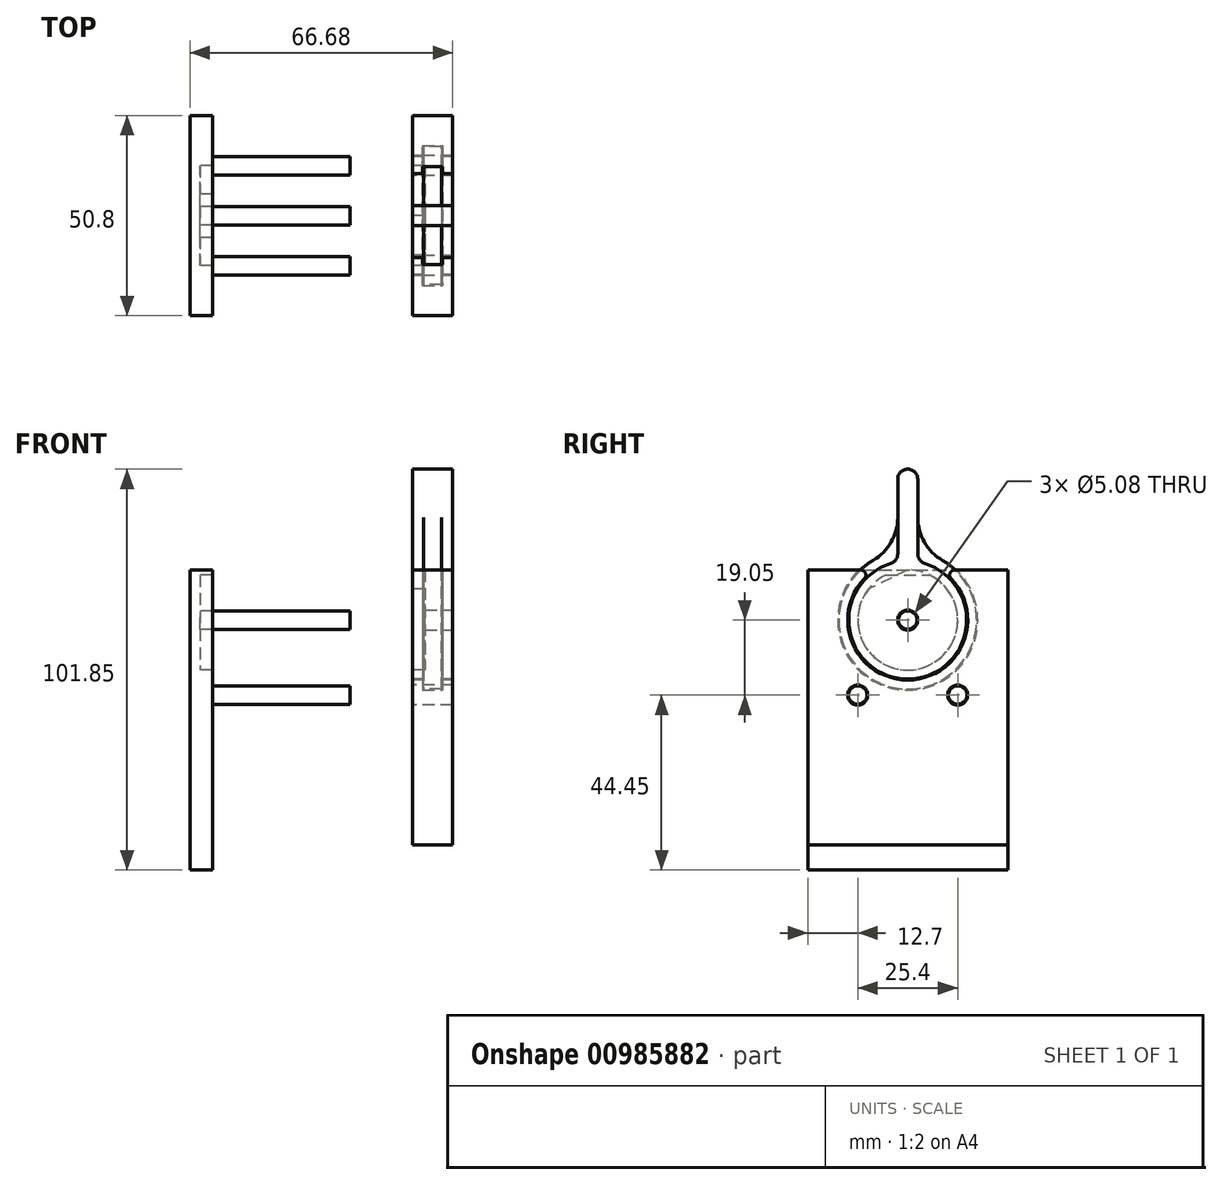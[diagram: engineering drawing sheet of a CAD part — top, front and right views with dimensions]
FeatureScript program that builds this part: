
annotation { "Feature Type Name" : "Feature", "Feature Type Description" : "" }
export const myFeature = defineFeature(function(context is Context, id is Id, definition is map)
    precondition{}
    {
        {
            var Q0;
            Q0=qCreatedBy(makeId("Right.planeOp"),FACE);
            var sketch = newSketch(context, id + "F0", { "sketchPlane" : qUnion([Q0])});
            skCircle(sketch, "E0", {"center": v(0, 0) * mm, "radius": 2.35 * mm});
            skSolve(sketch);
        }
        {
            var Q0;
            Q0=makeQuery(id+"F0.imprint","IMPRINT",FACE,{"disambiguationData":[TD([[makeQuery(id+"F0.imprint","IMPRINT",EDGE,{"derivedFrom":sQuery(id+"F0.wireOp",EDGE,"E0")}),1.0]])]});
            extrude(context, id + "F1", {"entities" : qUnion([Q0]), "depth" : 38.1 * mm, "offsetDistance" : 25.4 * mm});
        }
        {
            var Q0;
            Q0=qCreatedBy(makeId("Right.planeOp"),FACE);
            var sketch = newSketch(context, id + "F2", { "sketchPlane" : qUnion([Q0])});
            skLineSegment(sketch, "E1.bottom", {"start": v(-25.4, -63.5) * mm, "end": v(25.4, -63.5) * mm});
            skLineSegment(sketch, "E1.top", {"start": v(-25.4, 12.7) * mm, "end": v(25.4, 12.7) * mm});
            skLineSegment(sketch, "E1.left", {"start": v(-25.4, -63.5) * mm, "end": v(-25.4, 12.7) * mm});
            skLineSegment(sketch, "E1.right", {"start": v(25.4, -63.5) * mm, "end": v(25.4, 12.7) * mm});
            skSolve(sketch);
        }
        {
            var Q0;
            Q0=makeQuery(id+"F2.imprint","IMPRINT",FACE,{"disambiguationData":[TD([[makeQuery(id+"F2.imprint","IMPRINT",EDGE,{"derivedFrom":sQuery(id+"F2.wireOp",EDGE,"E1.bottom")}),1.0]])]});
            extrude(context, id + "F3", {"entities" : qUnion([Q0]), "operationType" : NewBodyOperationType.ADD, "oppositeDirection" : true, "depth" : 2.54 * mm, "offsetDistance" : 25.4 * mm});
        }
        {
            var Q0;
            Q0=makeQuery(id+"F3.opExtrude","CAP_FACE",FACE,{"disambiguationData":[OSD([sQuery(id+"F2.wireOp",EDGE,"E1.bottom"),sQuery(id+"F2.wireOp",EDGE,"E1.top"),sQuery(id+"F2.wireOp",EDGE,"E1.left"),sQuery(id+"F2.wireOp",EDGE,"E1.right")])],"isStart":true});
            var sketch = newSketch(context, id + "F4", { "sketchPlane" : qUnion([Q0])});
            skCircle(sketch, "E2", {"center": v(0, 0) * mm, "radius": 12.7 * mm});
            skLineSegment(sketch, "E3", {"start": v(-5.54, 11.43) * mm, "end": v(5.54, 11.43) * mm});
            skSolve(sketch);
        }
        {
            var Q0;
            Q0=makeQuery(id+"F4.imprint","IMPRINT",FACE,{"disambiguationData":[TD([[makeQuery(id+"F4.imprint","IMPRINT",EDGE,{"derivedFrom":makeQuery(id+"F3.opExtrude","CAP_EDGE",EDGE,{"disambiguationData":[OSD([sQuery(id+"F2.wireOp",EDGE,"E1.bottom")])],"isStart":true})}),1.0]])]});
            var Q1;
            {var subQ0=sQuery(id+"F4.wireOp",EDGE,"E3");Q1=makeQuery(id+"F4.imprint","IMPRINT",FACE,{"disambiguationData":[TD([[makeQuery(id+"F4.imprint","IMPRINT",EDGE,{"derivedFrom":subQ0}),1.0]])]});}
            extrude(context, id + "F5", {"entities" : qUnion([Q0, Q1]), "operationType" : NewBodyOperationType.ADD, "depth" : 3.17 * mm, "offsetDistance" : 25.4 * mm});
        }
        {
            var Q0;
            Q0=makeQuery(id+"F5.opExtrude","CAP_FACE",FACE,{"disambiguationData":[OSD([sQuery(id+"F2.wireOp",EDGE,"E1.bottom"),sQuery(id+"F2.wireOp",EDGE,"E1.top"),sQuery(id+"F2.wireOp",EDGE,"E1.left"),sQuery(id+"F2.wireOp",EDGE,"E1.right"),sQuery(id+"F4.wireOp",EDGE,"E2"),sQuery(id+"F4.wireOp",EDGE,"E3")])],"isStart":false});
            var sketch = newSketch(context, id + "F6", { "sketchPlane" : qUnion([Q0])});
            skCircle(sketch, "E4", {"center": v(-12.7, -19.05) * mm, "radius": 2.35 * mm});
            skCircle(sketch, "E5", {"center": v(12.7, -19.05) * mm, "radius": 2.35 * mm});
            skSolve(sketch);
        }
        {
            var Q0;
            Q0=makeQuery(id+"F6.imprint","IMPRINT",FACE,{"disambiguationData":[TD([[makeQuery(id+"F6.imprint","IMPRINT",EDGE,{"derivedFrom":sQuery(id+"F6.wireOp",EDGE,"E4")}),1.0]])]});
            var Q1;
            Q1=makeQuery(id+"F6.imprint","IMPRINT",FACE,{"disambiguationData":[TD([[makeQuery(id+"F6.imprint","IMPRINT",EDGE,{"derivedFrom":sQuery(id+"F6.wireOp",EDGE,"E5")}),1.0]])]});
            var Q2;
            Q2=makeQuery(id+"F1.opExtrude","CAP_FACE",FACE,{"disambiguationData":[OSD([sQuery(id+"F0.wireOp",EDGE,"E0")])],"isStart":false});
            extrude(context, id + "F7", {"entities" : qUnion([Q0, Q1]), "operationType" : NewBodyOperationType.ADD, "endBound" : BoundingType.UP_TO_SURFACE, "depth" : 25.4 * mm, "endBoundEntityFace" : qUnion([Q2]), "offsetDistance" : 25.4 * mm});
        }
        {
            var Q0;
            Q0=makeQuery(id+"F5.opExtrude","CAP_FACE",FACE,{"disambiguationData":[OSD([sQuery(id+"F2.wireOp",EDGE,"E1.bottom"),sQuery(id+"F2.wireOp",EDGE,"E1.top"),sQuery(id+"F2.wireOp",EDGE,"E1.left"),sQuery(id+"F2.wireOp",EDGE,"E1.right"),sQuery(id+"F4.wireOp",EDGE,"E2"),sQuery(id+"F4.wireOp",EDGE,"E3")])],"isStart":false});
            cPlane(context, id + "F8", {"entities" : qUnion([Q0]), "cplaneType" : CPlaneType.OFFSET, "offset" : 50.8 * mm, "width" : 152.4 * mm, "height" : 152.4 * mm});
        }
        {
            var Q0;
            Q0=qCreatedBy(id+"F8.planeOp",FACE);
            var sketch = newSketch(context, id + "F9", { "sketchPlane" : qUnion([Q0])});
            skLineSegment(sketch, "E6.bottom", {"start": v(-25.4, -57.15) * mm, "end": v(25.4, -57.15) * mm});
            skLineSegment(sketch, "E6.top", {"start": v(-25.4, 12.7) * mm, "end": v(25.4, 12.7) * mm});
            skLineSegment(sketch, "E6.left", {"start": v(-25.4, -57.15) * mm, "end": v(-25.4, 12.7) * mm});
            skLineSegment(sketch, "E6.right", {"start": v(25.4, -57.15) * mm, "end": v(25.4, 12.7) * mm});
            skCircle(sketch, "E7.0", {"center": v(0, 0) * mm, "radius": 2.35 * mm});
            skCircle(sketch, "E8.0.0", {"center": v(12.7, -19.05) * mm, "radius": 2.35 * mm});
            skCircle(sketch, "E9.0.0", {"center": v(-12.7, -19.05) * mm, "radius": 2.35 * mm});
            skCircle(sketch, "E10", {"center": v(12.7, -19.05) * mm, "radius": 2.54 * mm});
            skCircle(sketch, "E11", {"center": v(-12.7, -19.05) * mm, "radius": 2.54 * mm});
            skCircle(sketch, "E12", {"center": v(0, 0) * mm, "radius": 15.24 * mm});
            skSolve(sketch);
        }
        {
            var Q0;
            Q0=makeQuery(id+"F9.imprint","IMPRINT",FACE,{"disambiguationData":[TD([[makeQuery(id+"F9.imprint","IMPRINT",EDGE,{"derivedFrom":sQuery(id+"F9.wireOp",EDGE,"E6.bottom")}),1.0]])]});
            extrude(context, id + "F10", {"entities" : qUnion([Q0]), "depth" : 10.16 * mm, "offsetDistance" : 25.4 * mm});
        }
        {
            var Q0;
            {var subQ0=sQuery(id+"F9.wireOp",EDGE,"E12");var subQ1=sQuery(id+"F9.wireOp",EDGE,"E6.top");Q0=makeQuery(id+"F10.opExtrude","SWEPT_EDGE",EDGE,{"disambiguationData":[OSD([subQ1,subQ0]),TDD([makeQuery(id+"F9.imprint","INTERSECT",VERTEX,{"disambiguationData":[OD(1.0)],"derivedFrom":[subQ1,subQ0]})])]});}
            var Q1;
            {var subQ0=sQuery(id+"F9.wireOp",EDGE,"E12");var subQ1=sQuery(id+"F9.wireOp",EDGE,"E6.top");Q1=makeQuery(id+"F10.opExtrude","SWEPT_EDGE",EDGE,{"disambiguationData":[OSD([subQ1,subQ0]),TDD([makeQuery(id+"F9.imprint","INTERSECT",VERTEX,{"disambiguationData":[OD(0.0)],"derivedFrom":[subQ1,subQ0]})])]});}
            fillet(context, id + "F11", {"entities" : qUnion([Q0, Q1]), "radius" : 1.27 * mm, "tangentPropagation" : true, "allowEdgeOverflow" : false});
        }
        {
            var Q0;
            Q0=qCreatedBy(makeId("Top.planeOp"),FACE);
            var sketch = newSketch(context, id + "F12", { "sketchPlane" : qUnion([Q0])});
            skLineSegment(sketch, "E13.bottom", {"start": v(56.52, 17.78) * mm, "end": v(61.6, 17.78) * mm});
            skLineSegment(sketch, "E13.top", {"start": v(56.52, 8.52) * mm, "end": v(61.6, 8.52) * mm});
            skLineSegment(sketch, "E13.left", {"start": v(56.52, 17.78) * mm, "end": v(56.52, 8.52) * mm});
            skLineSegment(sketch, "E13.right", {"start": v(61.6, 17.78) * mm, "end": v(61.6, 8.52) * mm});
            skLineSegment(sketch, "E14", {"start": v(30.1, 15.24) * mm, "end": v(40.26, 15.24) * mm});
            skLineSegment(sketch, "E15", {"start": v(0, 2.35) * mm, "end": v(38.1, 2.35) * mm});
            skLineSegment(sketch, "E16", {"start": v(38.1, -2.35) * mm, "end": v(0, -2.35) * mm});
            skPoint(sketch, "E17.0", {"position": v(0, 0) * mm});
            skLineSegment(sketch, "E18", {"start": v(0, 0) * mm, "end": v(56.77, 0) * mm, "construction": true});
            skSolve(sketch);
        }
        {
            var Q0;
            {var subQ0=sQuery(id+"F12.wireOp",EDGE,"E13.bottom");Q0=makeQuery(id+"F12.imprint","IMPRINT",FACE,{"disambiguationData":[TD([[makeQuery(id+"F12.imprint","IMPRINT",EDGE,{"derivedFrom":subQ0}),-1.0]])]});}
            var Q1;
            Q1=sQuery(id+"F12.wireOp",EDGE,"E18");
            revolve(context, id + "F13", {"operationType" : NewBodyOperationType.REMOVE, "surfaceOperationType" : NewSurfaceOperationType.NEW, "entities" : qUnion([Q0]), "axis" : qUnion([Q1]), "revolveType" : RevolveType.FULL, "oppositeDirection" : true});
        }
        {
            var Q0;
            Q0=qCreatedBy(makeId("Top.planeOp"),FACE);
            var sketch = newSketch(context, id + "F14", { "sketchPlane" : qUnion([Q0])});
            skLineSegment(sketch, "E19", {"start": v(32.64, 17.78) * mm, "end": v(37.72, 17.78) * mm});
            skLineSegment(sketch, "E20", {"start": v(30.1, 15.24) * mm, "end": v(32.64, 15.24) * mm});
            skLineSegment(sketch, "E21", {"start": v(37.72, 15.24) * mm, "end": v(40.26, 15.24) * mm});
            skLineSegment(sketch, "E22.0.0", {"start": v(56.52, 10.64) * mm, "end": v(56.52, 10.64) * mm});
            skLineSegment(sketch, "E22.0.1", {"start": v(56.52, 17.78) * mm, "end": v(56.52, -17.78) * mm});
            skLineSegment(sketch, "E22.0.2", {"start": v(56.52, -10.64) * mm, "end": v(56.52, -11.91) * mm});
            skLineSegment(sketch, "E22.0.3", {"start": v(56.52, 17.78) * mm, "end": v(56.52, -17.78) * mm});
            skLineSegment(sketch, "E23.0.0", {"start": v(61.6, -17.78) * mm, "end": v(61.6, 17.78) * mm});
            skLineSegment(sketch, "E23.0.1", {"start": v(61.6, -10.64) * mm, "end": v(61.6, -11.91) * mm});
            skLineSegment(sketch, "E23.0.2", {"start": v(61.6, -17.78) * mm, "end": v(61.6, 17.78) * mm});
            skLineSegment(sketch, "E23.0.3", {"start": v(61.6, 10.64) * mm, "end": v(61.6, 10.64) * mm});
            skLineSegment(sketch, "E24", {"start": v(53.98, 14.99) * mm, "end": v(56.77, 14.99) * mm});
            skLineSegment(sketch, "E25", {"start": v(56.77, 14.99) * mm, "end": v(56.77, 17.53) * mm});
            skLineSegment(sketch, "E26", {"start": v(56.77, 17.53) * mm, "end": v(61.34, 17.53) * mm});
            skLineSegment(sketch, "E27", {"start": v(61.34, 17.53) * mm, "end": v(61.34, 14.99) * mm});
            skLineSegment(sketch, "E28", {"start": v(61.34, 14.99) * mm, "end": v(64.13, 14.99) * mm});
            skLineSegment(sketch, "E29", {"start": v(53.98, 14.99) * mm, "end": v(53.98, 0) * mm});
            skLineSegment(sketch, "E30", {"start": v(53.98, 0) * mm, "end": v(64.13, 0) * mm});
            skLineSegment(sketch, "E31", {"start": v(64.13, 0) * mm, "end": v(64.13, 14.99) * mm});
            skSolve(sketch);
        }
        {
            var Q0;
            {var subQ5=sQuery(id+"F14.wireOp",EDGE,"E29");Q0=makeQuery(id+"F14.imprint","IMPRINT",FACE,{"disambiguationData":[TD([[makeQuery(id+"F14.imprint","IMPRINT",EDGE,{"derivedFrom":subQ5}),1.0]])]});}
            var Q1;
            {var subQ0=sQuery(id+"F14.wireOp",EDGE,"E25");Q1=makeQuery(id+"F14.imprint","IMPRINT",FACE,{"disambiguationData":[TD([[makeQuery(id+"F14.imprint","IMPRINT",EDGE,{"derivedFrom":subQ0}),-1.0]])]});}
            var Q2;
            {var subQ5=sQuery(id+"F14.wireOp",EDGE,"E31");Q2=makeQuery(id+"F14.imprint","IMPRINT",FACE,{"disambiguationData":[TD([[makeQuery(id+"F14.imprint","IMPRINT",EDGE,{"derivedFrom":subQ5}),1.0]])]});}
            var Q3;
            Q3=sQuery(id+"F14.wireOp",EDGE,"E30");
            revolve(context, id + "F15", {"surfaceOperationType" : NewSurfaceOperationType.NEW, "entities" : qUnion([Q0, Q1, Q2]), "axis" : qUnion([Q3]), "revolveType" : RevolveType.FULL});
        }
        {
            var Q0;
            Q0=makeQuery(id+"F15.opRevolve","SWEPT_FACE",FACE,{"disambiguationData":[OSD([sQuery(id+"F14.wireOp",EDGE,"E31")])]});
            var sketch = newSketch(context, id + "F16", { "sketchPlane" : qUnion([Q0])});
            skCircle(sketch, "E32", {"center": v(0, 0) * mm, "radius": 2.54 * mm});
            skSolve(sketch);
        }
        {
            var Q0;
            Q0=makeQuery(id+"F16.imprint","IMPRINT",FACE,{"disambiguationData":[TD([[makeQuery(id+"F16.imprint","IMPRINT",EDGE,{"derivedFrom":sQuery(id+"F16.wireOp",EDGE,"E32")}),1.0]])]});
            var Q1;
            Q1=makeQuery(id+"F15.opRevolve","SWEPT_FACE",FACE,{"disambiguationData":[OSD([sQuery(id+"F14.wireOp",EDGE,"E29")])]});
            extrude(context, id + "F17", {"entities" : qUnion([Q0]), "operationType" : NewBodyOperationType.REMOVE, "endBound" : BoundingType.UP_TO_SURFACE, "oppositeDirection" : true, "depth" : 25.4 * mm, "endBoundEntityFace" : qUnion([Q1]), "offsetDistance" : 25.4 * mm});
        }
        {
            var Q0;
            Q0=makeQuery(id+"F15.opRevolve","SWEPT_FACE",FACE,{"disambiguationData":[OSD([sQuery(id+"F14.wireOp",EDGE,"E29")])]});
            var sketch = newSketch(context, id + "F18", { "sketchPlane" : qUnion([Q0])});
            skCircle(sketch, "E33", {"center": v(0, 0) * mm, "radius": 12.7 * mm});
            skLineSegment(sketch, "E34", {"start": v(0, 12.7) * mm, "end": v(9.96, 7.87) * mm});
            skSolve(sketch);
        }
        {
            var Q0;
            Q0=makeQuery(id+"F18.imprint","IMPRINT",FACE,{"disambiguationData":[TD([[makeQuery(id+"F18.imprint","IMPRINT",EDGE,{"derivedFrom":sQuery(id+"F18.wireOp",EDGE,"9eb1fb30-74b1-4e65-bc14-25f69d5678ca.0.0")}),-1.0]])]});
            var Q1;
            {var subQ0=sQuery(id+"F18.wireOp",EDGE,"E34");Q1=makeQuery(id+"F18.imprint","IMPRINT",FACE,{"disambiguationData":[TD([[makeQuery(id+"F18.imprint","IMPRINT",EDGE,{"derivedFrom":subQ0}),-1.0]])]});}
            extrude(context, id + "F19", {"entities" : qUnion([Q0, Q1]), "operationType" : NewBodyOperationType.REMOVE, "oppositeDirection" : true, "depth" : 3.17 * mm, "offsetDistance" : 25.4 * mm});
        }
        {
            var Q0;
            Q0=qCreatedBy(makeId("Top.planeOp"),FACE);
            cPlane(context, id + "F20", {"entities" : qUnion([Q0]), "cplaneType" : CPlaneType.OFFSET, "offset" : 12.95 * mm, "width" : 152.4 * mm, "height" : 152.4 * mm});
        }
        {
            var Q0;
            Q0=qCreatedBy(id+"F20.planeOp",FACE);
            var sketch = newSketch(context, id + "F21", { "sketchPlane" : qUnion([Q0])});
            skLineSegment(sketch, "E35.0", {"start": v(53.98, -14.99) * mm, "end": v(53.98, 14.99) * mm});
            skLineSegment(sketch, "E36.0", {"start": v(64.13, -14.99) * mm, "end": v(64.13, 14.99) * mm});
            skLineSegment(sketch, "E37.bottom", {"start": v(53.98, 2.54) * mm, "end": v(64.13, 2.54) * mm});
            skLineSegment(sketch, "E37.top", {"start": v(53.98, -2.54) * mm, "end": v(64.13, -2.54) * mm});
            skLineSegment(sketch, "E37.left", {"start": v(53.98, 2.54) * mm, "end": v(53.98, -2.54) * mm});
            skLineSegment(sketch, "E37.right", {"start": v(64.13, 2.54) * mm, "end": v(64.13, -2.54) * mm});
            skSolve(sketch);
        }
        {
            var Q0;
            {var subQ0=sQuery(id+"F21.wireOp",EDGE,"E37.bottom");Q0=makeQuery(id+"F21.imprint","IMPRINT",FACE,{"disambiguationData":[TD([[makeQuery(id+"F21.imprint","IMPRINT",EDGE,{"derivedFrom":subQ0}),-1.0]])]});}
            extrude(context, id + "F22", {"entities" : qUnion([Q0]), "operationType" : NewBodyOperationType.ADD, "depth" : 25.4 * mm, "offsetDistance" : 25.4 * mm});
        }
        {
            var Q0;
            Q0=makeQuery(id+"F22.boolean.opBoolean","INTERSECT",EDGE,{"derivedFrom":[makeQuery(id+"F15.opRevolve","SWEPT_FACE",FACE,{"disambiguationData":[OSD([sQuery(id+"F14.wireOp",EDGE,"E28")])]}),makeQuery(id+"F22.opExtrude","SWEPT_FACE",FACE,{"disambiguationData":[OSD([sQuery(id+"F21.wireOp",EDGE,"E37.top")])]})]});
            var Q1;
            Q1=makeQuery(id+"F22.boolean.opBoolean","INTERSECT",EDGE,{"derivedFrom":[makeQuery(id+"F15.opRevolve","SWEPT_FACE",FACE,{"disambiguationData":[OSD([sQuery(id+"F14.wireOp",EDGE,"E28")])]}),makeQuery(id+"F22.opExtrude","SWEPT_FACE",FACE,{"disambiguationData":[OSD([sQuery(id+"F21.wireOp",EDGE,"E37.bottom")])]})]});
            var Q2;
            Q2=makeQuery(id+"F22.boolean.opBoolean","INTERSECT",EDGE,{"derivedFrom":[makeQuery(id+"F15.opRevolve","SWEPT_FACE",FACE,{"disambiguationData":[OSD([sQuery(id+"F14.wireOp",EDGE,"E24")])]}),makeQuery(id+"F22.opExtrude","SWEPT_FACE",FACE,{"disambiguationData":[OSD([sQuery(id+"F21.wireOp",EDGE,"E37.top")])]})]});
            var Q3;
            Q3=makeQuery(id+"F22.boolean.opBoolean","INTERSECT",EDGE,{"derivedFrom":[makeQuery(id+"F15.opRevolve","SWEPT_FACE",FACE,{"disambiguationData":[OSD([sQuery(id+"F14.wireOp",EDGE,"E24")])]}),makeQuery(id+"F22.opExtrude","SWEPT_FACE",FACE,{"disambiguationData":[OSD([sQuery(id+"F21.wireOp",EDGE,"E37.bottom")])]})]});
            fillet(context, id + "F23", {"entities" : qUnion([Q0, Q1, Q2, Q3]), "radius" : 2.54 * mm, "allowEdgeOverflow" : false});
        }
        {
            var Q0;
            Q0=makeQuery(id+"F22.boolean.opBoolean","INTERSECT",EDGE,{"derivedFrom":[makeQuery(id+"F15.opRevolve","SWEPT_FACE",FACE,{"disambiguationData":[OSD([sQuery(id+"F14.wireOp",EDGE,"E26")])]}),makeQuery(id+"F22.opExtrude","SWEPT_FACE",FACE,{"disambiguationData":[OSD([sQuery(id+"F21.wireOp",EDGE,"E37.bottom")])]})]});
            var Q1;
            Q1=makeQuery(id+"F22.boolean.opBoolean","INTERSECT",EDGE,{"derivedFrom":[makeQuery(id+"F15.opRevolve","SWEPT_FACE",FACE,{"disambiguationData":[OSD([sQuery(id+"F14.wireOp",EDGE,"E26")])]}),makeQuery(id+"F22.opExtrude","SWEPT_FACE",FACE,{"disambiguationData":[OSD([sQuery(id+"F21.wireOp",EDGE,"E37.top")])]})]});
            fillet(context, id + "F24", {"entities" : qUnion([Q0, Q1]), "radius" : 12.7 * mm, "tangentPropagation" : true, "allowEdgeOverflow" : false});
        }
        {
            var Q0;
            Q0=makeQuery(id+"F22.opExtrude","CAP_EDGE",EDGE,{"disambiguationData":[OSD([sQuery(id+"F21.wireOp",EDGE,"E37.top")])],"isStart":false});
            var Q1;
            Q1=makeQuery(id+"F22.opExtrude","CAP_EDGE",EDGE,{"disambiguationData":[OSD([sQuery(id+"F21.wireOp",EDGE,"E37.bottom")])],"isStart":false});
            fillet(context, id + "F25", {"entities" : qUnion([Q0, Q1]), "radius" : 2.54 * mm, "tangentPropagation" : true, "allowEdgeOverflow" : false});
        }
    });
